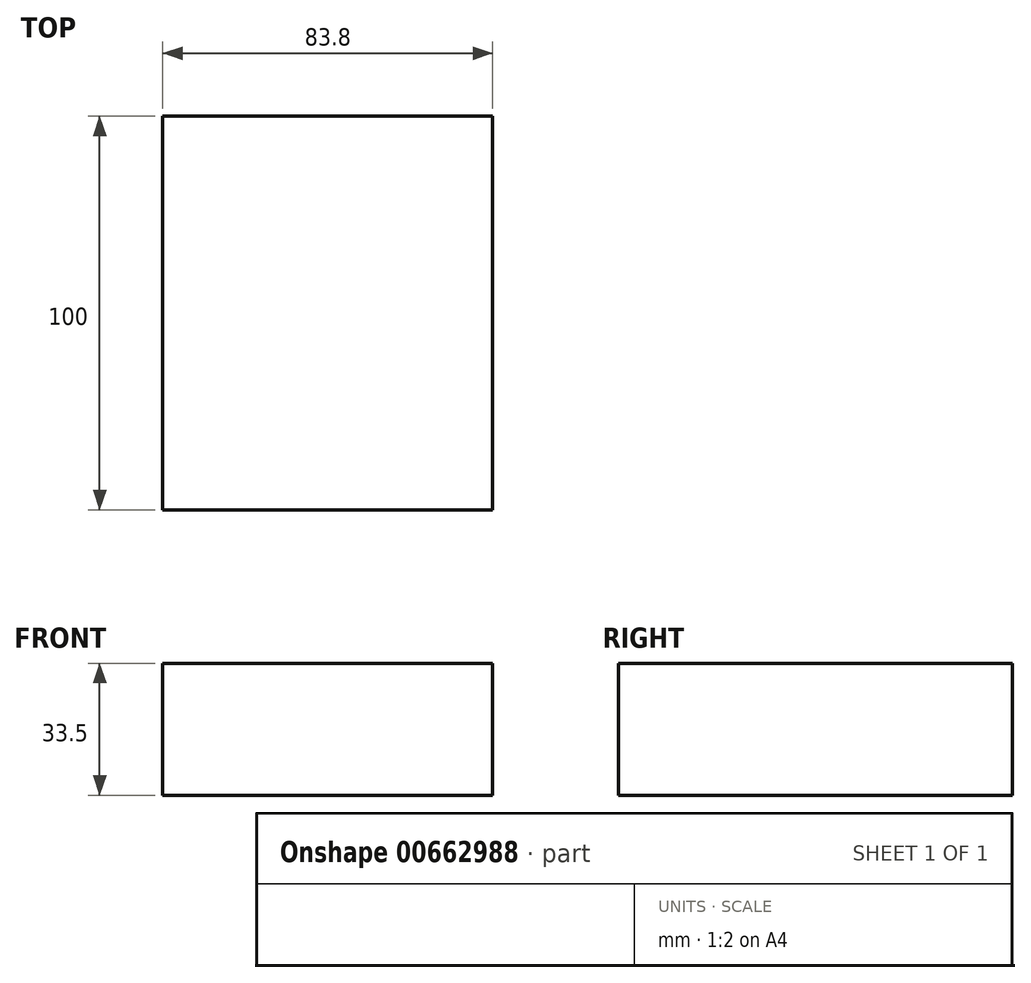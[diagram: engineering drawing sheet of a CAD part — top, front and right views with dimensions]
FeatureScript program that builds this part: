
annotation { "Feature Type Name" : "Feature", "Feature Type Description" : "" }
export const myFeature = defineFeature(function(context is Context, id is Id, definition is map)
    precondition{}
    {
        {
            var Q0;
            Q0=qCreatedBy(makeId("Front.planeOp"),FACE);
            var sketch = newSketch(context, id + "F0", { "sketchPlane" : qUnion([Q0])});
            skLineSegment(sketch, "E0.bottom", {"start": v(41.9, -16.75) * mm, "end": v(-41.9, -16.75) * mm});
            skLineSegment(sketch, "E0.top", {"start": v(41.9, 16.75) * mm, "end": v(-41.9, 16.75) * mm});
            skLineSegment(sketch, "E0.left", {"start": v(41.9, -16.75) * mm, "end": v(41.9, 16.75) * mm});
            skLineSegment(sketch, "E0.right", {"start": v(-41.9, -16.75) * mm, "end": v(-41.9, 16.75) * mm});
            skPoint(sketch, "E0.middle", {"position": v(0, 0) * mm});
            skSolve(sketch);
        }
        {
            var Q0;
            Q0=makeQuery(id+"F0.imprint","IMPRINT",FACE,{"disambiguationData":[TD([[makeQuery(id+"F0.imprint","IMPRINT",EDGE,{"derivedFrom":sQuery(id+"F0.wireOp",EDGE,"E0.bottom")}),-1.0]])]});
            extrude(context, id + "F1", {"entities" : qUnion([Q0]), "depth" : 100 * mm, "offsetDistance" : 25 * mm});
        }
    });
